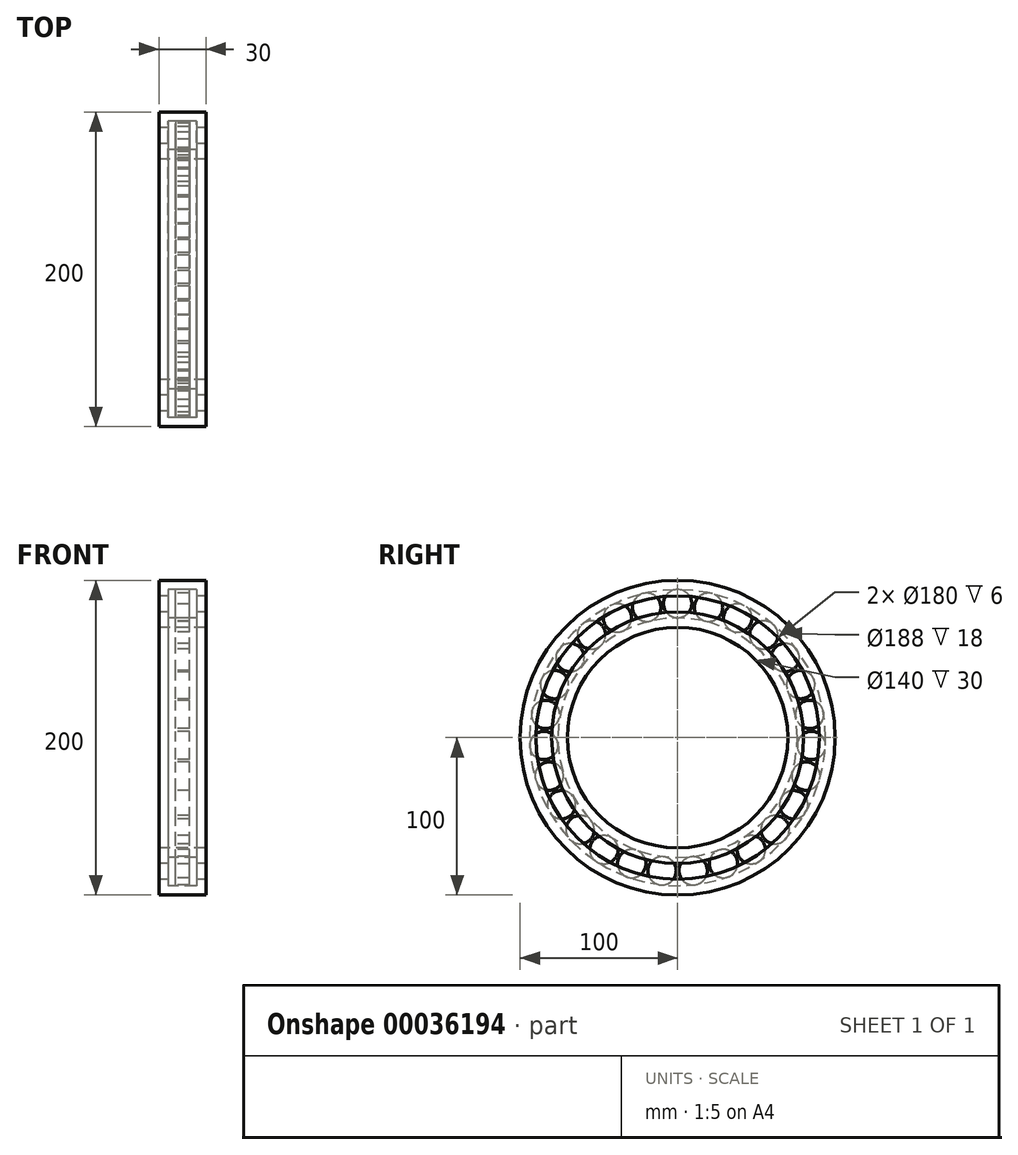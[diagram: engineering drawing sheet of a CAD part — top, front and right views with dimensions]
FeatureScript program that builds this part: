
annotation { "Feature Type Name" : "Feature", "Feature Type Description" : "" }
export const myFeature = defineFeature(function(context is Context, id is Id, definition is map)
    precondition{}
    {
        {
            var Q0;
            Q0=qCreatedBy(makeId("Front.planeOp"),FACE);
            var sketch = newSketch(context, id + "F0", { "sketchPlane" : qUnion([Q0])});
            skLineSegment(sketch, "E0", {"start": v(-106.42, 0) * mm, "end": v(108.4, 0) * mm});
            skLineSegment(sketch, "E1", {"start": v(0, 100) * mm, "end": v(15, 100) * mm});
            skLineSegment(sketch, "E2", {"start": v(0, 100) * mm, "end": v(-15, 100) * mm});
            skLineSegment(sketch, "E3", {"start": v(-15, 100) * mm, "end": v(-15, 90) * mm});
            skLineSegment(sketch, "E4", {"start": v(15, 100) * mm, "end": v(15, 90) * mm});
            skLineSegment(sketch, "E5", {"start": v(-15, 70) * mm, "end": v(0, 70) * mm});
            skLineSegment(sketch, "E6", {"start": v(15, 70) * mm, "end": v(0, 70) * mm});
            skLineSegment(sketch, "E7", {"start": v(0, 94) * mm, "end": v(-9, 94) * mm});
            skLineSegment(sketch, "E8", {"start": v(0, 94) * mm, "end": v(9, 94) * mm});
            skLineSegment(sketch, "E9", {"start": v(0, 76) * mm, "end": v(-9, 76) * mm});
            skLineSegment(sketch, "E10", {"start": v(0, 76) * mm, "end": v(9, 76) * mm});
            skLineSegment(sketch, "E11", {"start": v(-9, 94) * mm, "end": v(-9, 76) * mm});
            skLineSegment(sketch, "E12", {"start": v(9, 94) * mm, "end": v(9, 76) * mm});
            skLineSegment(sketch, "E13", {"start": v(-12.05, 90) * mm, "end": v(-15, 90) * mm});
            skLineSegment(sketch, "E14", {"start": v(-12.05, 90) * mm, "end": v(-9, 90) * mm});
            skLineSegment(sketch, "E15", {"start": v(-12.05, 80) * mm, "end": v(-9, 80) * mm});
            skLineSegment(sketch, "E16", {"start": v(-12.05, 80) * mm, "end": v(-15, 80) * mm});
            skLineSegment(sketch, "E17", {"start": v(11.93, 90) * mm, "end": v(15, 90) * mm});
            skLineSegment(sketch, "E18", {"start": v(11.93, 90) * mm, "end": v(9, 90) * mm});
            skLineSegment(sketch, "E19", {"start": v(11.93, 80) * mm, "end": v(9, 80) * mm});
            skLineSegment(sketch, "E20", {"start": v(11.93, 80) * mm, "end": v(15, 80) * mm});
            skLineSegment(sketch, "E21.trimOffspring", {"start": v(-15, 80) * mm, "end": v(-15, 70) * mm});
            skLineSegment(sketch, "E22.trimOffspring", {"start": v(15, 80) * mm, "end": v(15, 70) * mm});
            skPoint(sketch, "E23", {"position": v(0, 85) * mm});
            skSolve(sketch);
        }
        {
            var Q0;
            Q0=makeQuery(id+"F0.imprint","IMPRINT",FACE,{"disambiguationData":[TD([[makeQuery(id+"F0.imprint","IMPRINT",EDGE,{"derivedFrom":sQuery(id+"F0.wireOp",EDGE,"E1")}),-1.0]])]});
            var Q1;
            Q1=makeQuery(id+"F0.imprint","IMPRINT",FACE,{"disambiguationData":[TD([[makeQuery(id+"F0.imprint","IMPRINT",EDGE,{"derivedFrom":sQuery(id+"F0.wireOp",EDGE,"E5")}),1.0]])]});
            var Q2;
            Q2=sQuery(id+"F0.wireOp",EDGE,"E0");
            revolve(context, id + "F1", {"entities" : qUnion([Q0, Q1]), "axis" : qUnion([Q2]), "revolveType" : RevolveType.FULL});
        }
        {
            var Q0;
            Q0=qCreatedBy(makeId("Right.planeOp"),FACE);
            var sketch = newSketch(context, id + "F2", { "sketchPlane" : qUnion([Q0])});
            skCircle(sketch, "E24", {"center": v(0, 85.14) * mm, "radius": 9 * mm});
            skCircle(sketch, "E25.1.0", {"center": v(-19.63, 82.84) * mm, "radius": 9 * mm});
            skCircle(sketch, "E25.2.0", {"center": v(-38.2, 76.08) * mm, "radius": 9 * mm});
            skCircle(sketch, "E25.3.0", {"center": v(-54.72, 65.22) * mm, "radius": 9 * mm});
            skCircle(sketch, "E25.4.0", {"center": v(-68.29, 50.84) * mm, "radius": 9 * mm});
            skCircle(sketch, "E25.5.0", {"center": v(-78.17, 33.72) * mm, "radius": 9 * mm});
            skCircle(sketch, "E25.6.0", {"center": v(-83.84, 14.78) * mm, "radius": 9 * mm});
            skCircle(sketch, "E25.7.0", {"center": v(-85, -4.95) * mm, "radius": 9 * mm});
            skCircle(sketch, "E25.8.0", {"center": v(-81.56, -24.42) * mm, "radius": 9 * mm});
            skCircle(sketch, "E25.9.0", {"center": v(-73.73, -42.57) * mm, "radius": 9 * mm});
            skCircle(sketch, "E25.10.0", {"center": v(-61.93, -58.42) * mm, "radius": 9 * mm});
            skCircle(sketch, "E25.11.0", {"center": v(-46.78, -71.13) * mm, "radius": 9 * mm});
            skCircle(sketch, "E25.12.0", {"center": v(-29.12, -80) * mm, "radius": 9 * mm});
            skCircle(sketch, "E25.13.0", {"center": v(-9.88, -84.56) * mm, "radius": 9 * mm});
            skCircle(sketch, "E25.14.0", {"center": v(9.88, -84.56) * mm, "radius": 9 * mm});
            skCircle(sketch, "E25.15.0", {"center": v(29.12, -80) * mm, "radius": 9 * mm});
            skCircle(sketch, "E25.16.0", {"center": v(46.78, -71.13) * mm, "radius": 9 * mm});
            skCircle(sketch, "E25.17.0", {"center": v(61.93, -58.42) * mm, "radius": 9 * mm});
            skCircle(sketch, "E25.18.0", {"center": v(73.73, -42.57) * mm, "radius": 9 * mm});
            skCircle(sketch, "E25.19.0", {"center": v(81.56, -24.42) * mm, "radius": 9 * mm});
            skCircle(sketch, "E25.20.0", {"center": v(85, -4.95) * mm, "radius": 9 * mm});
            skCircle(sketch, "E25.21.0", {"center": v(83.84, 14.78) * mm, "radius": 9 * mm});
            skCircle(sketch, "E25.22.0", {"center": v(78.17, 33.72) * mm, "radius": 9 * mm});
            skCircle(sketch, "E25.23.0", {"center": v(68.29, 50.84) * mm, "radius": 9 * mm});
            skCircle(sketch, "E25.24.0", {"center": v(54.72, 65.22) * mm, "radius": 9 * mm});
            skCircle(sketch, "E25.25.0", {"center": v(38.2, 76.08) * mm, "radius": 9 * mm});
            skCircle(sketch, "E25.26.0", {"center": v(19.63, 82.84) * mm, "radius": 9 * mm});
            skPoint(sketch, "E25.center", {"position": v(0, 0) * mm});
            skSolve(sketch);
        }
        {
            var Q0;
            Q0=makeQuery(id+"F2.imprint","IMPRINT",FACE,{"disambiguationData":[TD([[makeQuery(id+"F2.imprint","IMPRINT",EDGE,{"derivedFrom":sQuery(id+"F2.wireOp",EDGE,"E24")}),1.0]])]});
            var Q1;
            Q1=makeQuery(id+"F2.imprint","IMPRINT",FACE,{"disambiguationData":[TD([[makeQuery(id+"F2.imprint","IMPRINT",EDGE,{"derivedFrom":sQuery(id+"F2.wireOp",EDGE,"E25.1.0")}),1.0]])]});
            var Q2;
            Q2=makeQuery(id+"F2.imprint","IMPRINT",FACE,{"disambiguationData":[TD([[makeQuery(id+"F2.imprint","IMPRINT",EDGE,{"derivedFrom":sQuery(id+"F2.wireOp",EDGE,"E25.2.0")}),1.0]])]});
            var Q3;
            Q3=makeQuery(id+"F2.imprint","IMPRINT",FACE,{"disambiguationData":[TD([[makeQuery(id+"F2.imprint","IMPRINT",EDGE,{"derivedFrom":sQuery(id+"F2.wireOp",EDGE,"E25.3.0")}),1.0]])]});
            var Q4;
            Q4=makeQuery(id+"F2.imprint","IMPRINT",FACE,{"disambiguationData":[TD([[makeQuery(id+"F2.imprint","IMPRINT",EDGE,{"derivedFrom":sQuery(id+"F2.wireOp",EDGE,"E25.4.0")}),1.0]])]});
            var Q5;
            Q5=makeQuery(id+"F2.imprint","IMPRINT",FACE,{"disambiguationData":[TD([[makeQuery(id+"F2.imprint","IMPRINT",EDGE,{"derivedFrom":sQuery(id+"F2.wireOp",EDGE,"E25.5.0")}),1.0]])]});
            var Q6;
            Q6=makeQuery(id+"F2.imprint","IMPRINT",FACE,{"disambiguationData":[TD([[makeQuery(id+"F2.imprint","IMPRINT",EDGE,{"derivedFrom":sQuery(id+"F2.wireOp",EDGE,"E25.6.0")}),1.0]])]});
            var Q7;
            Q7=makeQuery(id+"F2.imprint","IMPRINT",FACE,{"disambiguationData":[TD([[makeQuery(id+"F2.imprint","IMPRINT",EDGE,{"derivedFrom":sQuery(id+"F2.wireOp",EDGE,"E25.7.0")}),1.0]])]});
            var Q8;
            Q8=makeQuery(id+"F2.imprint","IMPRINT",FACE,{"disambiguationData":[TD([[makeQuery(id+"F2.imprint","IMPRINT",EDGE,{"derivedFrom":sQuery(id+"F2.wireOp",EDGE,"E25.8.0")}),1.0]])]});
            var Q9;
            Q9=makeQuery(id+"F2.imprint","IMPRINT",FACE,{"disambiguationData":[TD([[makeQuery(id+"F2.imprint","IMPRINT",EDGE,{"derivedFrom":sQuery(id+"F2.wireOp",EDGE,"E25.9.0")}),1.0]])]});
            var Q10;
            Q10=makeQuery(id+"F2.imprint","IMPRINT",FACE,{"disambiguationData":[TD([[makeQuery(id+"F2.imprint","IMPRINT",EDGE,{"derivedFrom":sQuery(id+"F2.wireOp",EDGE,"E25.10.0")}),1.0]])]});
            var Q11;
            Q11=makeQuery(id+"F2.imprint","IMPRINT",FACE,{"disambiguationData":[TD([[makeQuery(id+"F2.imprint","IMPRINT",EDGE,{"derivedFrom":sQuery(id+"F2.wireOp",EDGE,"E25.12.0")}),1.0]])]});
            var Q12;
            Q12=makeQuery(id+"F2.imprint","IMPRINT",FACE,{"disambiguationData":[TD([[makeQuery(id+"F2.imprint","IMPRINT",EDGE,{"derivedFrom":sQuery(id+"F2.wireOp",EDGE,"E25.11.0")}),1.0]])]});
            var Q13;
            Q13=makeQuery(id+"F2.imprint","IMPRINT",FACE,{"disambiguationData":[TD([[makeQuery(id+"F2.imprint","IMPRINT",EDGE,{"derivedFrom":sQuery(id+"F2.wireOp",EDGE,"E25.13.0")}),1.0]])]});
            var Q14;
            Q14=makeQuery(id+"F2.imprint","IMPRINT",FACE,{"disambiguationData":[TD([[makeQuery(id+"F2.imprint","IMPRINT",EDGE,{"derivedFrom":sQuery(id+"F2.wireOp",EDGE,"E25.14.0")}),1.0]])]});
            var Q15;
            Q15=makeQuery(id+"F2.imprint","IMPRINT",FACE,{"disambiguationData":[TD([[makeQuery(id+"F2.imprint","IMPRINT",EDGE,{"derivedFrom":sQuery(id+"F2.wireOp",EDGE,"E25.15.0")}),1.0]])]});
            var Q16;
            Q16=makeQuery(id+"F2.imprint","IMPRINT",FACE,{"disambiguationData":[TD([[makeQuery(id+"F2.imprint","IMPRINT",EDGE,{"derivedFrom":sQuery(id+"F2.wireOp",EDGE,"E25.16.0")}),1.0]])]});
            var Q17;
            Q17=makeQuery(id+"F2.imprint","IMPRINT",FACE,{"disambiguationData":[TD([[makeQuery(id+"F2.imprint","IMPRINT",EDGE,{"derivedFrom":sQuery(id+"F2.wireOp",EDGE,"E25.17.0")}),1.0]])]});
            var Q18;
            Q18=makeQuery(id+"F2.imprint","IMPRINT",FACE,{"disambiguationData":[TD([[makeQuery(id+"F2.imprint","IMPRINT",EDGE,{"derivedFrom":sQuery(id+"F2.wireOp",EDGE,"E25.18.0")}),1.0]])]});
            var Q19;
            Q19=makeQuery(id+"F2.imprint","IMPRINT",FACE,{"disambiguationData":[TD([[makeQuery(id+"F2.imprint","IMPRINT",EDGE,{"derivedFrom":sQuery(id+"F2.wireOp",EDGE,"E25.19.0")}),1.0]])]});
            var Q20;
            Q20=makeQuery(id+"F2.imprint","IMPRINT",FACE,{"disambiguationData":[TD([[makeQuery(id+"F2.imprint","IMPRINT",EDGE,{"derivedFrom":sQuery(id+"F2.wireOp",EDGE,"E25.20.0")}),1.0]])]});
            var Q21;
            Q21=makeQuery(id+"F2.imprint","IMPRINT",FACE,{"disambiguationData":[TD([[makeQuery(id+"F2.imprint","IMPRINT",EDGE,{"derivedFrom":sQuery(id+"F2.wireOp",EDGE,"E25.21.0")}),1.0]])]});
            var Q22;
            Q22=makeQuery(id+"F2.imprint","IMPRINT",FACE,{"disambiguationData":[TD([[makeQuery(id+"F2.imprint","IMPRINT",EDGE,{"derivedFrom":sQuery(id+"F2.wireOp",EDGE,"E25.22.0")}),1.0]])]});
            var Q23;
            Q23=makeQuery(id+"F2.imprint","IMPRINT",FACE,{"disambiguationData":[TD([[makeQuery(id+"F2.imprint","IMPRINT",EDGE,{"derivedFrom":sQuery(id+"F2.wireOp",EDGE,"E25.23.0")}),1.0]])]});
            var Q24;
            Q24=makeQuery(id+"F2.imprint","IMPRINT",FACE,{"disambiguationData":[TD([[makeQuery(id+"F2.imprint","IMPRINT",EDGE,{"derivedFrom":sQuery(id+"F2.wireOp",EDGE,"E25.24.0")}),1.0]])]});
            var Q25;
            Q25=makeQuery(id+"F2.imprint","IMPRINT",FACE,{"disambiguationData":[TD([[makeQuery(id+"F2.imprint","IMPRINT",EDGE,{"derivedFrom":sQuery(id+"F2.wireOp",EDGE,"E25.25.0")}),1.0]])]});
            var Q26;
            Q26=makeQuery(id+"F2.imprint","IMPRINT",FACE,{"disambiguationData":[TD([[makeQuery(id+"F2.imprint","IMPRINT",EDGE,{"derivedFrom":sQuery(id+"F2.wireOp",EDGE,"E25.26.0")}),1.0]])]});
            extrude(context, id + "F3", {"entities" : qUnion([Q0, Q1, Q2, Q3, Q4, Q5, Q6, Q7, Q8, Q9, Q10, Q11, Q12, Q13, Q14, Q15, Q16, Q17, Q18, Q19, Q20, Q21, Q22, Q23, Q24, Q25, Q26]), "endBound" : BoundingType.SYMMETRIC, "depth" : 9 * mm});
        }
    });
